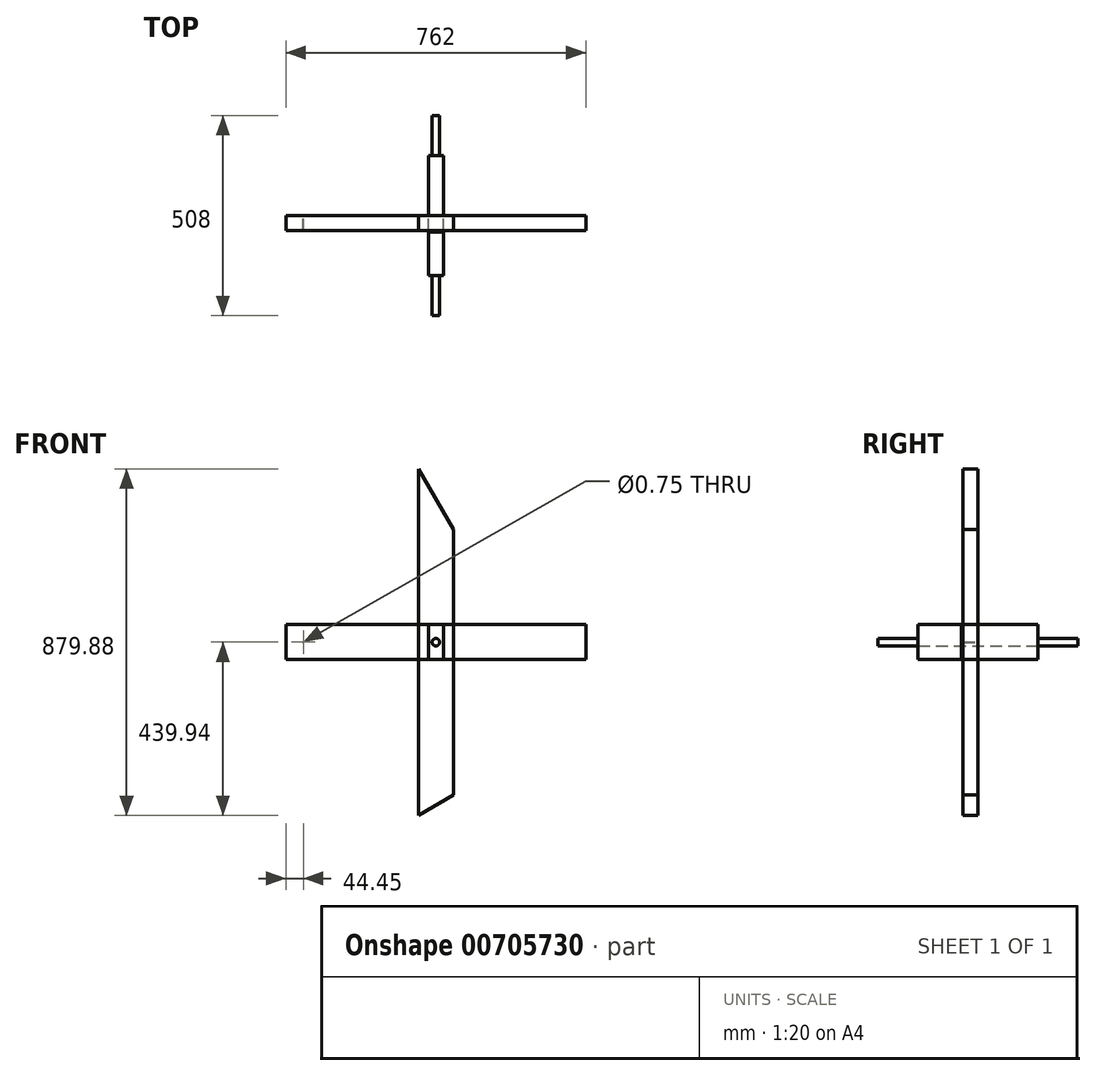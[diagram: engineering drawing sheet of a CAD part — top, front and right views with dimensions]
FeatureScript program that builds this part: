
annotation { "Feature Type Name" : "Feature", "Feature Type Description" : "" }
export const myFeature = defineFeature(function(context is Context, id is Id, definition is map)
    precondition{}
    {
        {
            assignVariable(context, id + "F0", {"name" : "AxleDiameter", "anyValue" : .75});
        }
        {
            assignVariable(context, id + "F1", {"name" : "Width", "anyValue" : 42});
        }
        {
            var Q0;
            Q0=qCreatedBy(makeId("Front.planeOp"),FACE);
            var sketch = newSketch(context, id + "F2", { "sketchPlane" : qUnion([Q0])});
            skLineSegment(sketch, "E0.bottom", {"start": v(19.05, -44.45) * mm, "end": v(-19.05, -44.45) * mm});
            skLineSegment(sketch, "E0.top", {"start": v(19.05, 44.45) * mm, "end": v(-19.05, 44.45) * mm});
            skLineSegment(sketch, "E0.left", {"start": v(19.05, -44.45) * mm, "end": v(19.05, 44.45) * mm});
            skLineSegment(sketch, "E0.right", {"start": v(-19.05, -44.45) * mm, "end": v(-19.05, 44.45) * mm});
            skPoint(sketch, "E0.middle", {"position": v(0, 0) * mm});
            skSolve(sketch);
        }
        {
            var Q0;
            Q0=makeQuery(id+"F2.imprint","IMPRINT",FACE,{"disambiguationData":[TD([[makeQuery(id+"F2.imprint","IMPRINT",EDGE,{"derivedFrom":sQuery(id+"F2.wireOp",EDGE,"E0.bottom")}),-1.0]])]});
            extrude(context, id + "F3", {"entities" : qUnion([Q0]), "endBound" : BoundingType.SYMMETRIC, "depth" : 304.8 * mm, "offsetDistance" : 25.4 * mm});
        }
        {
            var Q0;
            Q0=qCreatedBy(makeId("Front.planeOp"),FACE);
            var sketch = newSketch(context, id + "F4", { "sketchPlane" : qUnion([Q0])});
            skLineSegment(sketch, "E1.bottom", {"start": v(44.45, -439.94) * mm, "end": v(-44.45, -439.94) * mm});
            skLineSegment(sketch, "E1.top", {"start": v(44.45, 439.94) * mm, "end": v(-44.45, 439.94) * mm});
            skLineSegment(sketch, "E1.left", {"start": v(44.45, -439.94) * mm, "end": v(44.45, 439.94) * mm});
            skLineSegment(sketch, "E1.right", {"start": v(-44.45, -439.94) * mm, "end": v(-44.45, 439.94) * mm});
            skPoint(sketch, "E1.middle", {"position": v(0, 0) * mm});
            skLineSegment(sketch, "E2", {"start": v(-44.45, -439.94) * mm, "end": v(44.45, -388.61) * mm});
            skLineSegment(sketch, "E3", {"start": v(-44.45, 439.94) * mm, "end": v(44.45, 285.96) * mm});
            skSolve(sketch);
        }
        {
            var Q0;
            Q0=makeQuery(id+"F4.imprint","IMPRINT",FACE,{"disambiguationData":[TD([[makeQuery(id+"F4.imprint","IMPRINT",EDGE,{"derivedFrom":sQuery(id+"F4.wireOp",EDGE,"E1.right")}),-1.0]])]});
            extrude(context, id + "F5", {"entities" : qUnion([Q0]), "depth" : 38.1 * mm, "offsetDistance" : 25.4 * mm});
        }
        {
            var Q0;
            Q0=qCreatedBy(makeId("Front.planeOp"),FACE);
            var sketch = newSketch(context, id + "F6", { "sketchPlane" : qUnion([Q0])});
            skLineSegment(sketch, "E4.bottom", {"start": v(381, -44.45) * mm, "end": v(-381, -44.45) * mm});
            skLineSegment(sketch, "E4.top", {"start": v(381, 44.45) * mm, "end": v(-381, 44.45) * mm});
            skLineSegment(sketch, "E4.left", {"start": v(381, -44.45) * mm, "end": v(381, 44.45) * mm});
            skLineSegment(sketch, "E4.right", {"start": v(-381, -44.45) * mm, "end": v(-381, 44.45) * mm});
            skPoint(sketch, "E4.middle", {"position": v(0, 0) * mm});
            skPoint(sketch, "E5", {"position": v(-336.55, 0) * mm});
            skSolve(sketch);
        }
        {
            var Q0;
            Q0=makeQuery(id+"F6.imprint","IMPRINT",FACE,{"disambiguationData":[TD([[makeQuery(id+"F6.imprint","IMPRINT",EDGE,{"derivedFrom":sQuery(id+"F6.wireOp",EDGE,"E4.bottom")}),-1.0]])]});
            extrude(context, id + "F7", {"entities" : qUnion([Q0]), "depth" : 38.1 * mm, "offsetDistance" : 25.4 * mm});
        }
        {
            var Q0;
            Q0=sQuery(id+"F6.wireOp",VERTEX,"E5");
            var Q1;
            Q1=makeQuery(id+"F7.opExtrude","SWEPT_BODY",BODY,{"disambiguationData":[OSD([sQuery(id+"F6.wireOp",EDGE,"E4.bottom"),sQuery(id+"F6.wireOp",EDGE,"E4.top"),sQuery(id+"F6.wireOp",EDGE,"E4.left"),sQuery(id+"F6.wireOp",EDGE,"E4.right")])]});
            hole(context, id + "F8", {"style" : HoleStyle.SIMPLE, "endStyle" : HoleEndStyle.THROUGH, "oppositeDirection" : true, "holeDiameter" : (getVariable(context, 'AxleDiameter')) * mm, "majorDiameter" : 6.35 * mm, "isTappedThrough" : true, "tappedDepth" : 12.7 * mm, "tapClearance" : 3, "locations" : qUnion([Q0]), "scope" : qUnion([Q1])});
        }
        {
            var Q0;
            Q0=qCreatedBy(makeId("Front.planeOp"),FACE);
            var sketch = newSketch(context, id + "F9", { "sketchPlane" : qUnion([Q0])});
            skCircle(sketch, "E6", {"center": v(0, 0) * mm, "radius": 9.53 * mm});
            skSolve(sketch);
        }
        {
            var Q0;
            Q0=makeQuery(id+"F9.imprint","IMPRINT",FACE,{"disambiguationData":[TD([[makeQuery(id+"F9.imprint","IMPRINT",EDGE,{"derivedFrom":sQuery(id+"F9.wireOp",EDGE,"E6")}),1.0]])]});
            extrude(context, id + "F10", {"entities" : qUnion([Q0]), "endBound" : BoundingType.SYMMETRIC, "depth" : 508 * mm, "offsetDistance" : 25.4 * mm});
        }
        {
            var Q0;
            Q0 = qSketchRegion(id + "F2", true);
            extrude(context, id + "F11", {"entities" : qUnion([Q0]), "depth" : (getVariable(context, 'Width')) * mm, "offsetDistance" : 25.4 * mm});
        }
    });
